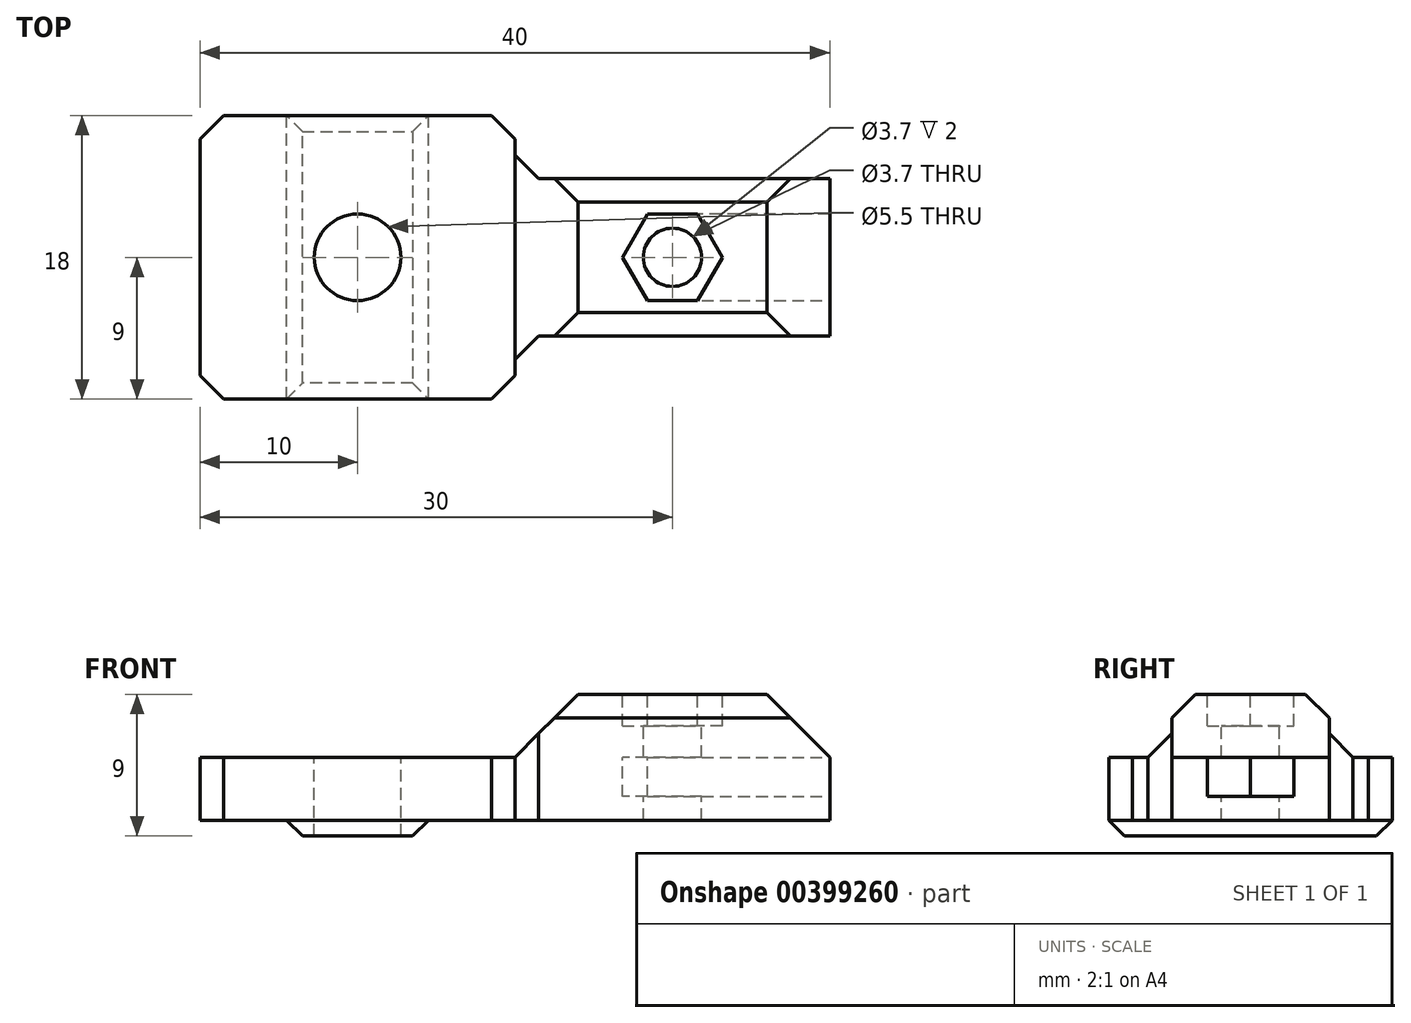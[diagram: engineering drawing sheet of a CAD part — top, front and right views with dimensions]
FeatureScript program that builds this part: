
annotation { "Feature Type Name" : "Feature", "Feature Type Description" : "" }
export const myFeature = defineFeature(function(context is Context, id is Id, definition is map)
    precondition{}
    {
        {
            var Q0;
            Q0=qCreatedBy(makeId("Top.planeOp"),FACE);
            var sketch = newSketch(context, id + "F0", { "sketchPlane" : qUnion([Q0])});
            skLineSegment(sketch, "E0.bottom", {"start": v(0, 0) * mm, "end": v(20, 0) * mm});
            skLineSegment(sketch, "E0.top", {"start": v(0, 18) * mm, "end": v(20, 18) * mm});
            skLineSegment(sketch, "E0.left", {"start": v(0, 0) * mm, "end": v(0, 18) * mm});
            skLineSegment(sketch, "E0.right", {"start": v(40, 4) * mm, "end": v(40, 14) * mm});
            skLineSegment(sketch, "E1", {"start": v(20, 18) * mm, "end": v(20, 14) * mm});
            skLineSegment(sketch, "E2", {"start": v(20, 14) * mm, "end": v(40, 14) * mm});
            skLineSegment(sketch, "E3", {"start": v(0, 9) * mm, "end": v(40, 9) * mm, "construction": true});
            skLineSegment(sketch, "E4.MirrorCS", {"start": v(20, 4) * mm, "end": v(40, 4) * mm});
            skLineSegment(sketch, "E5.MirrorCS", {"start": v(20, 0) * mm, "end": v(20, 4) * mm});
            skPoint(sketch, "E6.orphan", {"position": v(40, 18) * mm});
            skPoint(sketch, "E7.orphan", {"position": v(40, 0) * mm});
            skSolve(sketch);
        }
        {
            var Q0;
            Q0 = qSketchRegion(id + "F0", true);
            extrude(context, id + "F1", {"entities" : qUnion([Q0]), "depth" : 4 * mm});
        }
        {
            var Q0;
            Q0=makeQuery(id+"F1.opExtrude","CAP_FACE",FACE,{"disambiguationData":[OSD([sQuery(id+"F0.wireOp",EDGE,"E0.bottom"),sQuery(id+"F0.wireOp",EDGE,"E0.top"),sQuery(id+"F0.wireOp",EDGE,"E0.left"),sQuery(id+"F0.wireOp",EDGE,"E0.right"),sQuery(id+"F0.wireOp",EDGE,"E1"),sQuery(id+"F0.wireOp",EDGE,"E2"),sQuery(id+"F0.wireOp",EDGE,"E4.MirrorCS"),sQuery(id+"F0.wireOp",EDGE,"E5.MirrorCS")])],"isStart":true});
            var sketch = newSketch(context, id + "F2", { "sketchPlane" : qUnion([Q0])});
            skLineSegment(sketch, "E8.bottom", {"start": v(5.5, 0) * mm, "end": v(14.5, 0) * mm});
            skLineSegment(sketch, "E8.top", {"start": v(5.5, -18) * mm, "end": v(14.5, -18) * mm});
            skLineSegment(sketch, "E8.left", {"start": v(5.5, 0) * mm, "end": v(5.5, -18) * mm});
            skLineSegment(sketch, "E8.right", {"start": v(14.5, 0) * mm, "end": v(14.5, -18) * mm});
            skSolve(sketch);
        }
        {
            var Q0;
            Q0=makeQuery(id+"F2.imprint","IMPRINT",FACE,{"disambiguationData":[TD([[makeQuery(id+"F2.imprint","IMPRINT",EDGE,{"derivedFrom":sQuery(id+"F2.wireOp",EDGE,"E8.bottom")}),-1.0]])]});
            extrude(context, id + "F3", {"entities" : qUnion([Q0]), "operationType" : NewBodyOperationType.ADD, "depth" : 1 * mm});
        }
        {
            var Q0;
            Q0=makeQuery(id+"F3.opExtrude","CAP_FACE",FACE,{"disambiguationData":[OSD([sQuery(id+"F2.wireOp",EDGE,"E8.bottom"),sQuery(id+"F2.wireOp",EDGE,"E8.top"),sQuery(id+"F2.wireOp",EDGE,"E8.left"),sQuery(id+"F2.wireOp",EDGE,"E8.right")])],"isStart":false});
            chamfer(context, id + "F4", {"entities" : qUnion([Q0]), "width" : 1 * mm, "tangentPropagation" : true});
        }
        {
            var Q0;
            Q0=makeQuery(id+"F1.opExtrude","CAP_FACE",FACE,{"disambiguationData":[OSD([sQuery(id+"F0.wireOp",EDGE,"E0.bottom"),sQuery(id+"F0.wireOp",EDGE,"E0.top"),sQuery(id+"F0.wireOp",EDGE,"E0.left"),sQuery(id+"F0.wireOp",EDGE,"E0.right"),sQuery(id+"F0.wireOp",EDGE,"E1"),sQuery(id+"F0.wireOp",EDGE,"E2"),sQuery(id+"F0.wireOp",EDGE,"E4.MirrorCS"),sQuery(id+"F0.wireOp",EDGE,"E5.MirrorCS")])],"isStart":false});
            var sketch = newSketch(context, id + "F5", { "sketchPlane" : qUnion([Q0])});
            skLineSegment(sketch, "E9.0", {"start": v(20, 14) * mm, "end": v(40, 14) * mm});
            skLineSegment(sketch, "E10.0", {"start": v(40, 4) * mm, "end": v(40, 14) * mm});
            skLineSegment(sketch, "E11.0", {"start": v(20, 4) * mm, "end": v(40, 4) * mm});
            skLineSegment(sketch, "E12", {"start": v(20, 14) * mm, "end": v(20, 4) * mm});
            skSolve(sketch);
        }
        {
            var Q0;
            Q0=makeQuery(id+"F5.imprint","IMPRINT",FACE,{"disambiguationData":[TD([[makeQuery(id+"F5.imprint","IMPRINT",EDGE,{"derivedFrom":sQuery(id+"F5.wireOp",EDGE,"E9.0")}),-1.0]])]});
            extrude(context, id + "F6", {"entities" : qUnion([Q0]), "operationType" : NewBodyOperationType.ADD, "depth" : 4 * mm});
        }
        {
            var Q0;
            Q0=makeQuery(id+"F1.opExtrude","CAP_FACE",FACE,{"disambiguationData":[OSD([sQuery(id+"F0.wireOp",EDGE,"E0.bottom"),sQuery(id+"F0.wireOp",EDGE,"E0.top"),sQuery(id+"F0.wireOp",EDGE,"E0.left"),sQuery(id+"F0.wireOp",EDGE,"E0.right"),sQuery(id+"F0.wireOp",EDGE,"E1"),sQuery(id+"F0.wireOp",EDGE,"E2"),sQuery(id+"F0.wireOp",EDGE,"E4.MirrorCS"),sQuery(id+"F0.wireOp",EDGE,"E5.MirrorCS")])],"isStart":false});
            var sketch = newSketch(context, id + "F7", { "sketchPlane" : qUnion([Q0])});
            skLineSegment(sketch, "E13.0.0", {"start": v(40, 14) * mm, "end": v(20, 14) * mm, "construction": true});
            skLineSegment(sketch, "E13.0.1", {"start": v(20, 14) * mm, "end": v(20, 4) * mm, "construction": true});
            skLineSegment(sketch, "E13.0.2", {"start": v(20, 4) * mm, "end": v(40, 4) * mm, "construction": true});
            skLineSegment(sketch, "E13.0.3", {"start": v(40, 4) * mm, "end": v(40, 14) * mm, "construction": true});
            skCircle(sketch, "E14.cCircle", {"center": v(30, 9) * mm, "radius": 2.75 * mm, "construction": true});
            skPoint(sketch, "E14.cCircle.centerSnap0", {"position": v(40, 9) * mm});
            skPoint(sketch, "E14.cCircle.centerSnap1", {"position": v(30, 14) * mm});
            skLineSegment(sketch, "E14.0", {"start": v(28.41, 11.75) * mm, "end": v(31.59, 11.75) * mm, "construction": true});
            skLineSegment(sketch, "E14.1", {"start": v(31.59, 11.75) * mm, "end": v(33.18, 9) * mm, "construction": true});
            skLineSegment(sketch, "E14.2", {"start": v(33.18, 9) * mm, "end": v(31.59, 6.25) * mm, "construction": true});
            skLineSegment(sketch, "E14.3", {"start": v(31.59, 6.25) * mm, "end": v(28.41, 6.25) * mm, "construction": true});
            skLineSegment(sketch, "E14.4", {"start": v(28.41, 6.25) * mm, "end": v(26.82, 9) * mm});
            skLineSegment(sketch, "E14.5", {"start": v(26.82, 9) * mm, "end": v(28.41, 11.75) * mm});
            skPoint(sketch, "E14.0.midPoint", {"position": v(30, 11.75) * mm});
            skLineSegment(sketch, "E15", {"start": v(28.41, 6.25) * mm, "end": v(40, 6.25) * mm});
            skLineSegment(sketch, "E16", {"start": v(40, 6.25) * mm, "end": v(40, 11.75) * mm});
            skLineSegment(sketch, "E17", {"start": v(40, 11.75) * mm, "end": v(28.41, 11.75) * mm});
            skSolve(sketch);
        }
        {
            var Q0;
            Q0 = qSketchRegion(id + "F7", true);
            extrude(context, id + "F8", {"entities" : qUnion([Q0]), "operationType" : NewBodyOperationType.REMOVE, "oppositeDirection" : true, "depth" : 2.5 * mm});
        }
        {
            var Q0;
            Q0=makeQuery(id+"F6.opExtrude","CAP_EDGE",EDGE,{"disambiguationData":[OSD([sQuery(id+"F5.wireOp",EDGE,"E12")])],"isStart":false});
            var Q1;
            Q1=makeQuery(id+"F6.opExtrude","CAP_EDGE",EDGE,{"disambiguationData":[OSD([sQuery(id+"F5.wireOp",EDGE,"E10.0")])],"isStart":false});
            chamfer(context, id + "F9", {"entities" : qUnion([Q0, Q1]), "width" : 4 * mm, "tangentPropagation" : true});
        }
        {
            var Q0;
            Q0=makeQuery(id+"F6.opExtrude","CAP_FACE",FACE,{"disambiguationData":[OSD([sQuery(id+"F5.wireOp",EDGE,"E9.0"),sQuery(id+"F5.wireOp",EDGE,"E10.0"),sQuery(id+"F5.wireOp",EDGE,"E11.0"),sQuery(id+"F5.wireOp",EDGE,"E12")])],"isStart":false});
            var sketch = newSketch(context, id + "F10", { "sketchPlane" : qUnion([Q0])});
            skLineSegment(sketch, "E18.0.0", {"start": v(28.41, 11.75) * mm, "end": v(26.82, 9) * mm, "construction": true});
            skLineSegment(sketch, "E18.0.2", {"start": v(26.82, 9) * mm, "end": v(28.41, 11.75) * mm, "construction": true});
            skLineSegment(sketch, "E19.0.0", {"start": v(26.82, 9) * mm, "end": v(28.41, 6.25) * mm, "construction": true});
            skLineSegment(sketch, "E19.0.2", {"start": v(28.41, 6.25) * mm, "end": v(26.82, 9) * mm, "construction": true});
            skLineSegment(sketch, "E20", {"start": v(27.62, 10.38) * mm, "end": v(30, 9) * mm, "construction": true});
            skLineSegment(sketch, "E21", {"start": v(30, 9) * mm, "end": v(27.62, 7.63) * mm, "construction": true});
            skCircle(sketch, "E22.cCircle", {"center": v(30, 9) * mm, "radius": 2.75 * mm, "construction": true});
            skLineSegment(sketch, "E22.0", {"start": v(28.41, 11.75) * mm, "end": v(31.59, 11.75) * mm});
            skLineSegment(sketch, "E22.1", {"start": v(31.59, 11.75) * mm, "end": v(33.18, 9) * mm});
            skLineSegment(sketch, "E22.2", {"start": v(33.18, 9) * mm, "end": v(31.59, 6.25) * mm});
            skLineSegment(sketch, "E22.3", {"start": v(31.59, 6.25) * mm, "end": v(28.41, 6.25) * mm});
            skLineSegment(sketch, "E22.4", {"start": v(28.41, 6.25) * mm, "end": v(26.82, 9) * mm});
            skLineSegment(sketch, "E22.5", {"start": v(26.82, 9) * mm, "end": v(28.41, 11.75) * mm});
            skPoint(sketch, "E22.0.midPoint", {"position": v(30, 11.75) * mm});
            skSolve(sketch);
        }
        {
            var Q0;
            Q0 = qSketchRegion(id + "F10", true);
            extrude(context, id + "F11", {"entities" : qUnion([Q0]), "operationType" : NewBodyOperationType.REMOVE, "oppositeDirection" : true, "depth" : 2 * mm});
        }
        {
            var Q0;
            Q0=makeQuery(id+"F1.opExtrude","SWEPT_EDGE",EDGE,{"disambiguationData":[OSD([sQuery(id+"F0.wireOp",EDGE,"E0.top"),sQuery(id+"F0.wireOp",EDGE,"E0.left")])]});
            var Q1;
            Q1=makeQuery(id+"F1.opExtrude","SWEPT_EDGE",EDGE,{"disambiguationData":[OSD([sQuery(id+"F0.wireOp",EDGE,"E0.bottom"),sQuery(id+"F0.wireOp",EDGE,"E0.left")])]});
            var Q2;
            Q2=makeQuery(id+"F1.opExtrude","SWEPT_EDGE",EDGE,{"disambiguationData":[OSD([sQuery(id+"F0.wireOp",EDGE,"E0.bottom"),sQuery(id+"F0.wireOp",EDGE,"E5.MirrorCS")])]});
            var Q3;
            Q3=makeQuery(id+"F1.opExtrude","SWEPT_EDGE",EDGE,{"disambiguationData":[OSD([sQuery(id+"F0.wireOp",EDGE,"E0.top"),sQuery(id+"F0.wireOp",EDGE,"E1")])]});
            var Q4;
            Q4=makeQuery(id+"F6.opExtrude","CAP_EDGE",EDGE,{"disambiguationData":[OSD([sQuery(id+"F5.wireOp",EDGE,"E11.0")])],"isStart":false});
            var Q5;
            Q5=makeQuery(id+"F6.opExtrude","CAP_EDGE",EDGE,{"disambiguationData":[OSD([sQuery(id+"F5.wireOp",EDGE,"E9.0")])],"isStart":false});
            var Q6;
            Q6=makeQuery(id+"F1.opExtrude","SWEPT_EDGE",EDGE,{"disambiguationData":[OSD([sQuery(id+"F0.wireOp",EDGE,"E1"),sQuery(id+"F0.wireOp",EDGE,"E2")])]});
            var Q7;
            Q7=makeQuery(id+"F1.opExtrude","SWEPT_EDGE",EDGE,{"disambiguationData":[OSD([sQuery(id+"F0.wireOp",EDGE,"E4.MirrorCS"),sQuery(id+"F0.wireOp",EDGE,"E5.MirrorCS")])]});
            chamfer(context, id + "F12", {"entities" : qUnion([Q0, Q1, Q2, Q3, Q4, Q5, Q6, Q7]), "width" : 1.5 * mm, "tangentPropagation" : true});
        }
        {
            var Q0;
            Q0=makeQuery(id+"F11.boolean.opBoolean","COPY",FACE,{"derivedFrom":makeQuery(id+"F11.opExtrude","CAP_FACE",FACE,{"disambiguationData":[OSD([sQuery(id+"F10.wireOp",EDGE,"E22.0"),sQuery(id+"F10.wireOp",EDGE,"E22.1"),sQuery(id+"F10.wireOp",EDGE,"E22.2"),sQuery(id+"F10.wireOp",EDGE,"E22.3"),sQuery(id+"F10.wireOp",EDGE,"E22.4"),sQuery(id+"F10.wireOp",EDGE,"E22.5")])],"isStart":false})});
            var sketch = newSketch(context, id + "F13", { "sketchPlane" : qUnion([Q0])});
            skLineSegment(sketch, "E23.0.0", {"start": v(20, 15.5) * mm, "end": v(20, 16.5) * mm, "construction": true});
            skLineSegment(sketch, "E23.0.1", {"start": v(20, 16.5) * mm, "end": v(18.5, 18) * mm, "construction": true});
            skLineSegment(sketch, "E23.0.2", {"start": v(18.5, 18) * mm, "end": v(1.5, 18) * mm, "construction": true});
            skLineSegment(sketch, "E23.0.3", {"start": v(1.5, 18) * mm, "end": v(0, 16.5) * mm, "construction": true});
            skLineSegment(sketch, "E23.0.4", {"start": v(0, 16.5) * mm, "end": v(0, 1.5) * mm, "construction": true});
            skLineSegment(sketch, "E23.0.5", {"start": v(0, 1.5) * mm, "end": v(1.5, 0) * mm, "construction": true});
            skLineSegment(sketch, "E23.0.6", {"start": v(1.5, 0) * mm, "end": v(18.5, 0) * mm, "construction": true});
            skLineSegment(sketch, "E23.0.7", {"start": v(18.5, 0) * mm, "end": v(20, 1.5) * mm, "construction": true});
            skLineSegment(sketch, "E23.0.8", {"start": v(20, 1.5) * mm, "end": v(20, 2.5) * mm, "construction": true});
            skLineSegment(sketch, "E23.0.9", {"start": v(20, 2.5) * mm, "end": v(20, 15.5) * mm, "construction": true});
            skLineSegment(sketch, "E24.0.0", {"start": v(28.41, 11.75) * mm, "end": v(26.82, 9) * mm, "construction": true});
            skLineSegment(sketch, "E24.0.1", {"start": v(26.82, 9) * mm, "end": v(28.41, 6.25) * mm, "construction": true});
            skLineSegment(sketch, "E24.0.2", {"start": v(28.41, 6.25) * mm, "end": v(31.59, 6.25) * mm, "construction": true});
            skLineSegment(sketch, "E24.0.3", {"start": v(31.59, 6.25) * mm, "end": v(33.18, 9) * mm, "construction": true});
            skLineSegment(sketch, "E24.0.4", {"start": v(33.18, 9) * mm, "end": v(31.59, 11.75) * mm, "construction": true});
            skLineSegment(sketch, "E24.0.5", {"start": v(31.59, 11.75) * mm, "end": v(28.41, 11.75) * mm, "construction": true});
            skCircle(sketch, "E25", {"center": v(10, 9) * mm, "radius": 2.75 * mm});
            skPoint(sketch, "E25.centerSnap0", {"position": v(20, 9) * mm});
            skPoint(sketch, "E25.centerSnap1", {"position": v(10, 18) * mm});
            skCircle(sketch, "E26", {"center": v(30, 9) * mm, "radius": 1.85 * mm});
            skPoint(sketch, "E26.centerSnap0", {"position": v(30, 11.75) * mm});
            skSolve(sketch);
        }
        {
            var Q0;
            Q0 = qSketchRegion(id + "F13", true);
            extrude(context, id + "F14", {"entities" : qUnion([Q0]), "operationType" : NewBodyOperationType.REMOVE, "endBound" : BoundingType.THROUGH_ALL, "oppositeDirection" : true, "depth" : 25 * mm});
        }
    });
